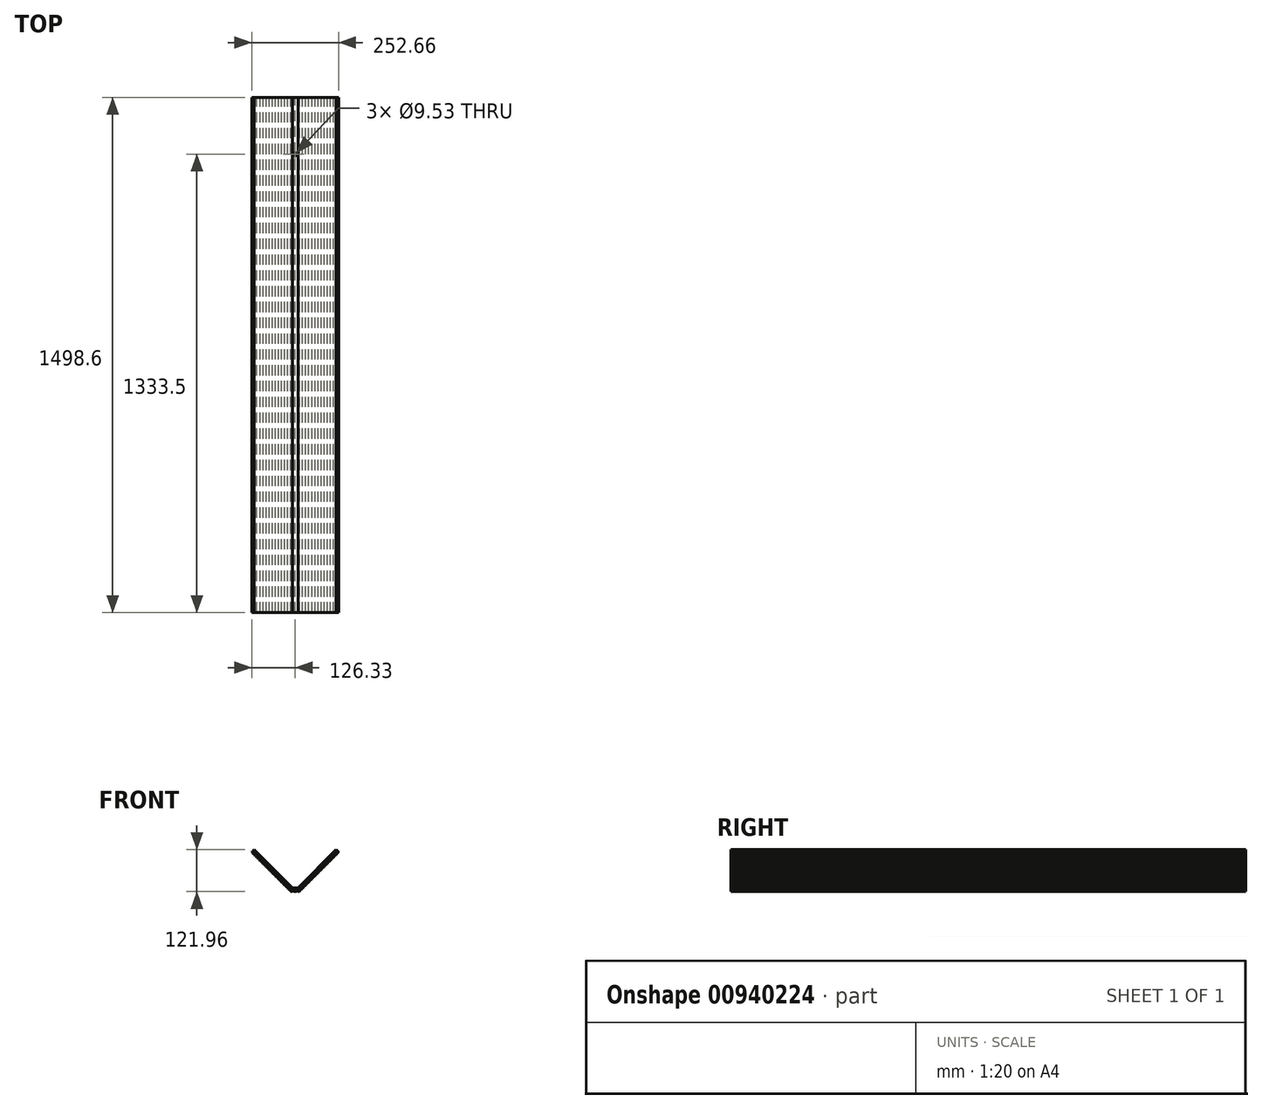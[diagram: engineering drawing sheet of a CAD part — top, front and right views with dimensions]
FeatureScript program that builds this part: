
annotation { "Feature Type Name" : "Feature", "Feature Type Description" : "" }
export const myFeature = defineFeature(function(context is Context, id is Id, definition is map)
    precondition{}
    {
        {
            var Q0;
            Q0=qCreatedBy(makeId("Front.planeOp"),FACE);
            var sketch = newSketch(context, id + "F0", { "sketchPlane" : qUnion([Q0])});
            skLineSegment(sketch, "E0", {"start": v(0, 0) * mm, "end": v(8.21, 0) * mm});
            skLineSegment(sketch, "E1", {"start": v(8.21, 0) * mm, "end": v(119.34, 111.13) * mm});
            skLineSegment(sketch, "E2", {"start": v(119.34, 111.13) * mm, "end": v(123.59, 106.88) * mm});
            skLineSegment(sketch, "E3", {"start": v(123.59, 106.88) * mm, "end": v(10.7, -6) * mm});
            skLineSegment(sketch, "E4", {"start": v(10.7, -6) * mm, "end": v(0, -6) * mm});
            skLineSegment(sketch, "E5", {"start": v(0, -7.02) * mm, "end": v(11.12, -7.02) * mm});
            skLineSegment(sketch, "E6", {"start": v(11.12, -7.02) * mm, "end": v(124.3, 106.16) * mm});
            skLineSegment(sketch, "E7", {"start": v(124.3, 106.16) * mm, "end": v(123.59, 106.88) * mm});
            skLineSegment(sketch, "E8", {"start": v(127, 103.47) * mm, "end": v(124.3, 106.16) * mm});
            skLineSegment(sketch, "E9", {"start": v(8.21, 0) * mm, "end": v(12.7, -10.83) * mm, "construction": true});
            skArc(sketch, "E10", {"start": v(12.7, -10.83) * mm, "mid": v(6.35, -9.65) * mm, "end": v(0, -10.83) * mm});
            skPoint(sketch, "E11.trimOffspring.start.orphan", {"position": v(127, 103.47) * mm});
            skLineSegment(sketch, "E12", {"start": v(0, -10.83) * mm, "end": v(12.7, -10.83) * mm, "construction": true});
            skLineSegment(sketch, "E13", {"start": v(12.7, -10.83) * mm, "end": v(120.46, 96.93) * mm, "construction": true});
            skArc(sketch, "E14.MirrorCS", {"start": v(12.7, -10.83) * mm, "mid": v(16.35, -5.5) * mm, "end": v(21.68, -1.85) * mm});
            skArc(sketch, "E15.1.0.0", {"start": v(21.68, -1.85) * mm, "mid": v(25.33, 3.47) * mm, "end": v(30.66, 7.13) * mm});
            skArc(sketch, "E15.2.0.0", {"start": v(30.66, 7.13) * mm, "mid": v(34.31, 12.45) * mm, "end": v(39.64, 16.1) * mm});
            skLineSegment(sketch, "E15.direction1", {"start": v(12.7, -10.83) * mm, "end": v(21.68, -1.85) * mm, "construction": true});
            skArc(sketch, "E16.0.3.0", {"start": v(39.64, 16.1) * mm, "mid": v(43.3, 21.43) * mm, "end": v(48.62, 25.09) * mm});
            skArc(sketch, "E16.0.4.0", {"start": v(48.62, 25.09) * mm, "mid": v(52.28, 30.41) * mm, "end": v(57.6, 34.07) * mm});
            skArc(sketch, "E16.0.5.0", {"start": v(57.6, 34.07) * mm, "mid": v(61.26, 39.4) * mm, "end": v(66.58, 43.05) * mm});
            skArc(sketch, "E16.0.6.0", {"start": v(66.58, 43.05) * mm, "mid": v(70.24, 48.37) * mm, "end": v(75.56, 52.03) * mm});
            skArc(sketch, "E16.0.7.0", {"start": v(75.56, 52.03) * mm, "mid": v(79.22, 57.35) * mm, "end": v(84.54, 61) * mm});
            skArc(sketch, "E16.0.8.0", {"start": v(84.54, 61) * mm, "mid": v(88.2, 66.34) * mm, "end": v(93.52, 69.99) * mm});
            skArc(sketch, "E16.0.9.0", {"start": v(93.52, 69.99) * mm, "mid": v(97.18, 75.32) * mm, "end": v(102.5, 78.97) * mm});
            skArc(sketch, "E16.0.10.0", {"start": v(102.5, 78.97) * mm, "mid": v(106.16, 84.3) * mm, "end": v(111.48, 87.95) * mm});
            skArc(sketch, "E16.0.11.0", {"start": v(111.48, 87.95) * mm, "mid": v(115.14, 93.28) * mm, "end": v(120.46, 96.93) * mm});
            skArc(sketch, "E16.0.12.0", {"start": v(120.46, 96.93) * mm, "mid": v(122.92, 100.93) * mm, "end": v(126.33, 104.13) * mm});
            skLineSegment(sketch, "E17.trimOffspring", {"start": v(127, 103.47) * mm, "end": v(127, 103.47) * mm, "construction": true});
            skLineSegment(sketch, "E18", {"start": v(0, 0) * mm, "end": v(0, -10.83) * mm, "construction": true});
            skLineSegment(sketch, "E19.MirrorCS", {"start": v(-127, 103.47) * mm, "end": v(-127, 103.47) * mm, "construction": true});
            skLineSegment(sketch, "E20.MirrorCS", {"start": v(-119.34, 111.13) * mm, "end": v(-123.59, 106.88) * mm});
            skLineSegment(sketch, "E21.MirrorCS", {"start": v(-127, 103.47) * mm, "end": v(-124.3, 106.16) * mm});
            skLineSegment(sketch, "E22.MirrorCS", {"start": v(-124.3, 106.16) * mm, "end": v(-123.59, 106.88) * mm});
            skLineSegment(sketch, "E23.MirrorCS", {"start": v(-8.21, 0) * mm, "end": v(-12.7, -10.83) * mm, "construction": true});
            skLineSegment(sketch, "E24.MirrorCS", {"start": v(0, -10.83) * mm, "end": v(-12.7, -10.83) * mm, "construction": true});
            skArc(sketch, "E25.MirrorCS", {"start": v(-102.5, 78.97) * mm, "mid": v(-106.16, 84.3) * mm, "end": v(-111.48, 87.95) * mm});
            skArc(sketch, "E26.MirrorCS", {"start": v(-120.46, 96.93) * mm, "mid": v(-122.92, 100.93) * mm, "end": v(-126.33, 104.13) * mm});
            skArc(sketch, "E27.MirrorCS", {"start": v(-111.48, 87.95) * mm, "mid": v(-115.14, 93.28) * mm, "end": v(-120.46, 96.93) * mm});
            skLineSegment(sketch, "E28.MirrorCS", {"start": v(-11.12, -7.02) * mm, "end": v(-124.3, 106.16) * mm});
            skArc(sketch, "E29.MirrorCS", {"start": v(-84.54, 61) * mm, "mid": v(-88.2, 66.34) * mm, "end": v(-93.52, 69.99) * mm});
            skArc(sketch, "E30.MirrorCS", {"start": v(-66.58, 43.05) * mm, "mid": v(-70.24, 48.37) * mm, "end": v(-75.56, 52.03) * mm});
            skArc(sketch, "E31.MirrorCS", {"start": v(-75.56, 52.03) * mm, "mid": v(-79.22, 57.35) * mm, "end": v(-84.54, 61) * mm});
            skLineSegment(sketch, "E32.MirrorCS", {"start": v(-123.59, 106.88) * mm, "end": v(-10.7, -6) * mm});
            skLineSegment(sketch, "E33.MirrorCS", {"start": v(0, 0) * mm, "end": v(-8.21, 0) * mm});
            skLineSegment(sketch, "E34.MirrorCS", {"start": v(-10.7, -6) * mm, "end": v(0, -6) * mm});
            skArc(sketch, "E35.MirrorCS", {"start": v(-93.52, 69.99) * mm, "mid": v(-97.18, 75.32) * mm, "end": v(-102.5, 78.97) * mm});
            skArc(sketch, "E36.MirrorCS", {"start": v(-12.7, -10.83) * mm, "mid": v(-16.35, -5.5) * mm, "end": v(-21.68, -1.85) * mm});
            skLineSegment(sketch, "E37.MirrorCS", {"start": v(-12.7, -10.83) * mm, "end": v(-21.68, -1.85) * mm, "construction": true});
            skArc(sketch, "E38.MirrorCS", {"start": v(-21.68, -1.85) * mm, "mid": v(-25.33, 3.47) * mm, "end": v(-30.66, 7.13) * mm});
            skArc(sketch, "E39.MirrorCS", {"start": v(-30.66, 7.13) * mm, "mid": v(-34.31, 12.45) * mm, "end": v(-39.64, 16.1) * mm});
            skArc(sketch, "E40.MirrorCS", {"start": v(-57.6, 34.07) * mm, "mid": v(-61.26, 39.4) * mm, "end": v(-66.58, 43.05) * mm});
            skPoint(sketch, "E41.MirrorP", {"position": v(-127, 103.47) * mm});
            skArc(sketch, "E42.MirrorCS", {"start": v(-39.64, 16.1) * mm, "mid": v(-43.3, 21.43) * mm, "end": v(-48.62, 25.09) * mm});
            skArc(sketch, "E43.MirrorCS", {"start": v(-48.62, 25.09) * mm, "mid": v(-52.28, 30.41) * mm, "end": v(-57.6, 34.07) * mm});
            skLineSegment(sketch, "E44.MirrorCS", {"start": v(0, -7.02) * mm, "end": v(-11.12, -7.02) * mm});
            skLineSegment(sketch, "E45.MirrorCS", {"start": v(-8.21, 0) * mm, "end": v(-119.34, 111.13) * mm});
            skArc(sketch, "E46.MirrorCS", {"start": v(-12.7, -10.83) * mm, "mid": v(-6.35, -9.65) * mm, "end": v(0, -10.83) * mm});
            skSolve(sketch);
        }
        {
            var Q0;
            Q0=makeQuery(id+"F0.imprint","IMPRINT",FACE,{"disambiguationData":[TD([[makeQuery(id+"F0.imprint","IMPRINT",EDGE,{"derivedFrom":sQuery(id+"F0.wireOp",EDGE,"E0")}),-1.0]])]});
            extrude(context, id + "F1", {"entities" : qUnion([Q0]), "depth" : 1498.6 * mm, "offsetDistance" : 25.4 * mm, "symmetric" : true});
        }
        {
            var Q0;
            Q0=makeQuery(id+"F0.imprint","IMPRINT",FACE,{"disambiguationData":[TD([[makeQuery(id+"F0.imprint","IMPRINT",EDGE,{"derivedFrom":sQuery(id+"F0.wireOp",EDGE,"E3")}),1.0]])]});
            extrude(context, id + "F2", {"entities" : qUnion([Q0]), "depth" : 1498.6 * mm, "offsetDistance" : 25.4 * mm, "symmetric" : true});
        }
        {
            var Q0;
            Q0=makeQuery(id+"F0.imprint","IMPRINT",FACE,{"disambiguationData":[TD([[makeQuery(id+"F0.imprint","IMPRINT",EDGE,{"derivedFrom":sQuery(id+"F0.wireOp",EDGE,"E5")}),-1.0]])]});
            extrude(context, id + "F3", {"entities" : qUnion([Q0]), "depth" : 1498.6 * mm, "offsetDistance" : 25.4 * mm, "symmetric" : true});
        }
        {
            var Q0;
            Q0=qCreatedBy(makeId("Top.planeOp"),FACE);
            var sketch = newSketch(context, id + "F4", { "sketchPlane" : qUnion([Q0])});
            skLineSegment(sketch, "E47", {"start": v(0, 374.65) * mm, "end": v(0, -374.65) * mm, "construction": true});
            skPoint(sketch, "E48", {"position": v(0, 0) * mm});
            skCircle(sketch, "E49", {"center": v(0, 584.2) * mm, "radius": 4.76 * mm});
            skLineSegment(sketch, "E50", {"start": v(0, 0) * mm, "end": v(-13.94, 0) * mm, "construction": true});
            skCircle(sketch, "E51.MirrorC", {"center": v(0, -584.2) * mm, "radius": 4.76 * mm});
            skSolve(sketch);
        }
        {
            var Q0;
            Q0=makeQuery(id+"F4.imprint","IMPRINT",FACE,{"disambiguationData":[TD([[makeQuery(id+"F4.imprint","IMPRINT",EDGE,{"derivedFrom":sQuery(id+"F4.wireOp",EDGE,"E49")}),1.0]])]});
            var Q1;
            Q1=makeQuery(id+"F4.imprint","IMPRINT",FACE,{"disambiguationData":[TD([[makeQuery(id+"F4.imprint","IMPRINT",EDGE,{"derivedFrom":sQuery(id+"F4.wireOp",EDGE,"E51.MirrorC")}),-1.0]])]});
            var Q2;
            Q2=sQuery(id+"F4.wireOp",EDGE,"E49");
            var Q3;
            Q3=sQuery(id+"F4.wireOp",EDGE,"E51.MirrorC");
            extrude(context, id + "F5", {"entities" : qUnion([Q0, Q1]), "operationType" : NewBodyOperationType.REMOVE, "surfaceEntities" : qUnion([Q2, Q3]), "endBound" : BoundingType.THROUGH_ALL, "oppositeDirection" : true, "depth" : 96.77 * mm, "offsetDistance" : 25.4 * mm});
        }
    });
